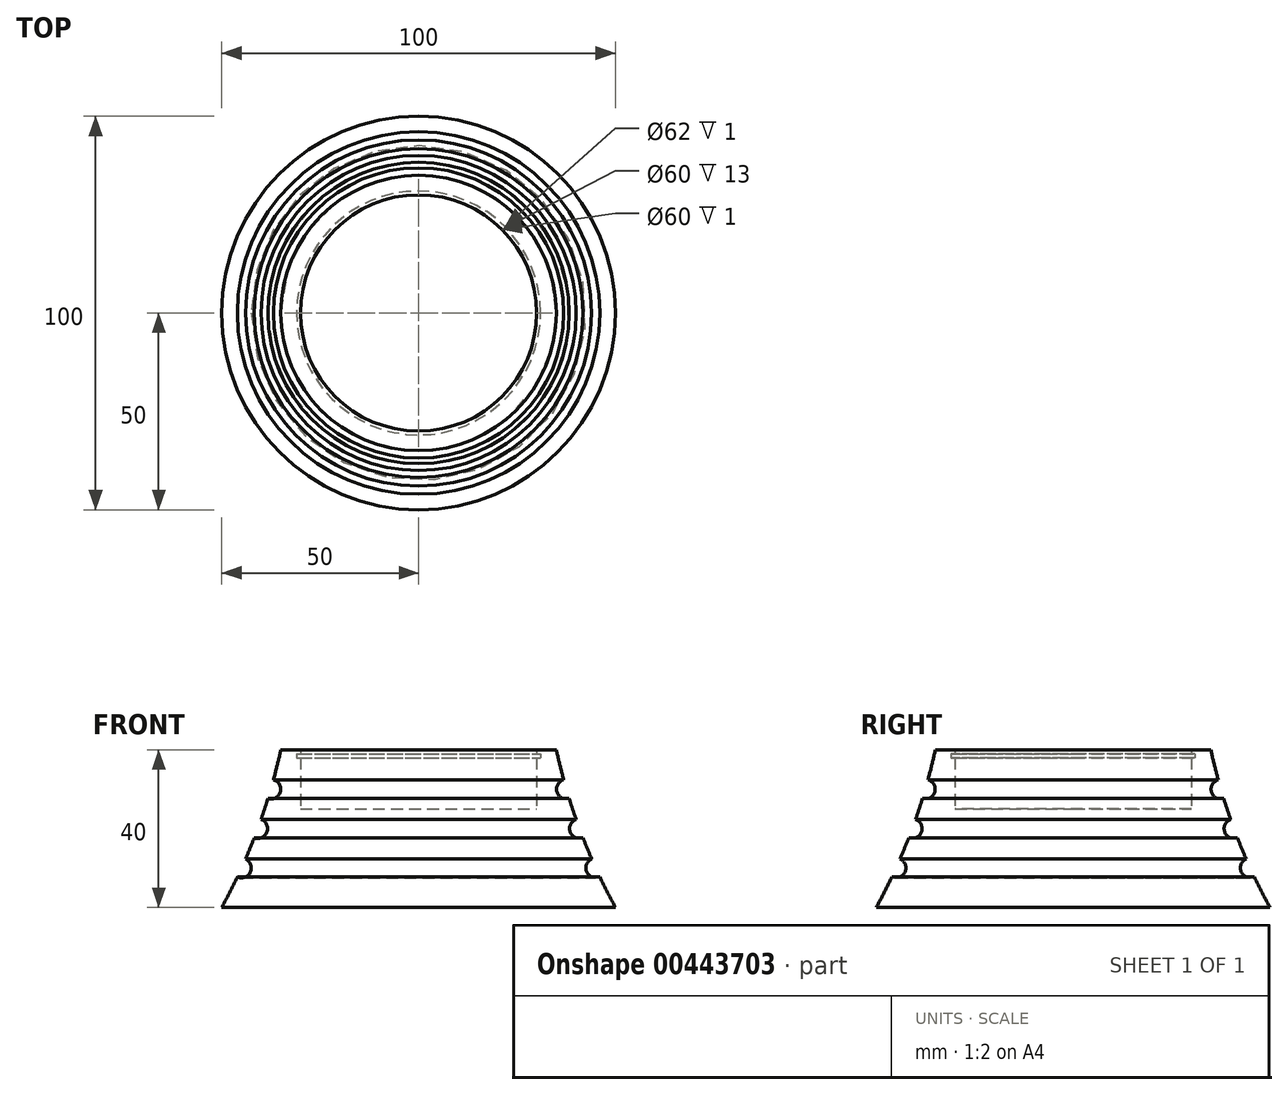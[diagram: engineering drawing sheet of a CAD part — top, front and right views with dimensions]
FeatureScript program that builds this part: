
annotation { "Feature Type Name" : "Feature", "Feature Type Description" : "" }
export const myFeature = defineFeature(function(context is Context, id is Id, definition is map)
    precondition{}
    {
        {
            var Q0;
            Q0=qCreatedBy(makeId("Front.planeOp"),FACE);
            var sketch = newSketch(context, id + "F0", { "sketchPlane" : qUnion([Q0])});
            skLineSegment(sketch, "E0", {"start": v(0, 0) * mm, "end": v(0, 25) * mm});
            skLineSegment(sketch, "E1", {"start": v(0, 25) * mm, "end": v(30, 25) * mm});
            skLineSegment(sketch, "E2", {"start": v(30, 25) * mm, "end": v(30, 38) * mm});
            skLineSegment(sketch, "E3", {"start": v(30, 40) * mm, "end": v(35, 40) * mm});
            skLineSegment(sketch, "E4", {"start": v(0, 0) * mm, "end": v(50, 0) * mm});
            skArc(sketch, "E5", {"start": v(35, 40) * mm, "mid": v(35.89, 36.2) * mm, "end": v(36.87, 32.4) * mm});
            skLineSegment(sketch, "E6.bottom", {"start": v(30, 39) * mm, "end": v(31, 39) * mm});
            skLineSegment(sketch, "E6.top", {"start": v(30, 38) * mm, "end": v(31, 38) * mm});
            skLineSegment(sketch, "E6.right", {"start": v(31, 39) * mm, "end": v(31, 38) * mm});
            skLineSegment(sketch, "E7.trimOffspring", {"start": v(30, 39) * mm, "end": v(30, 40) * mm});
            skArc(sketch, "E8", {"start": v(36.87, 32.4) * mm, "mid": v(35.16, 29.3) * mm, "end": v(38.28, 27.6) * mm});
            skArc(sketch, "E9", {"start": v(40.02, 22.35) * mm, "mid": v(38.52, 19.13) * mm, "end": v(41.76, 17.66) * mm});
            skArc(sketch, "E10", {"start": v(43.97, 12.28) * mm, "mid": v(42.72, 8.96) * mm, "end": v(46.05, 7.73) * mm});
            skArc(sketch, "E11.trimOffspring", {"start": v(38.28, 27.6) * mm, "mid": v(39.12, 24.97) * mm, "end": v(40.02, 22.35) * mm});
            skArc(sketch, "E12.trimOffspring", {"start": v(41.76, 17.66) * mm, "mid": v(42.84, 14.96) * mm, "end": v(43.97, 12.28) * mm});
            skArc(sketch, "E13.trimOffspring", {"start": v(46.05, 7.73) * mm, "mid": v(47.97, 3.84) * mm, "end": v(50, 0) * mm});
            skSolve(sketch);
        }
        {
            var Q0;
            Q0 = qSketchRegion(id + "F0", true);
            var Q1;
            Q1=sQuery(id+"F0.wireOp",EDGE,"E0");
            revolve(context, id + "F1", {"entities" : qUnion([Q0]), "axis" : qUnion([Q1]), "revolveType" : RevolveType.FULL});
        }
    });
